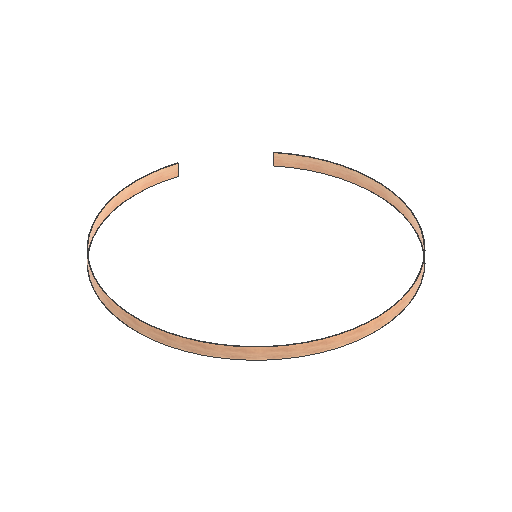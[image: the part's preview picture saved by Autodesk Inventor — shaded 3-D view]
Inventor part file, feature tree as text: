
AUTODESK INVENTOR PART (.ipt)
format: ipt  version: 2021 (Build 250183000, 183)  size: 118,272 bytes
history: native  units: mm
features: other x4, extrude x2, sketch x2, reference x2
ambient origin geometry x8: Origin, YZ Plane, XZ Plane, XY Plane, X Axis, Y Axis, Z Axis, Center Point
bodies: Solid1 (feature_tree)
feature tree (10):
  extrude  "Extrusion1"  Depth=2070.38mm
  extrude  "Extrusion2"  Depth=100.0mm TaperAngle=0.0deg
  sketch  "Sketch1"  dims[d0=2062.38mm d1=2070.38mm]
  sketch  "Sketch2"  dims[d2=100.0mm d3=0.0mm d4=100.0mm d5=0.0mm]
  reference  "Reference1"
  reference  "Reference2"
  other  "Full Scale Assembly.iam"
  other  "Disc B Assembly:1"
  other  "Platform B4:1"
  other  "Platform B1:1"
